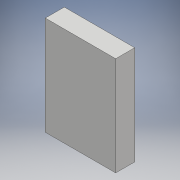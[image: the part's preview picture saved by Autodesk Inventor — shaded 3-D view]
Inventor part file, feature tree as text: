
AUTODESK INVENTOR PART (.ipt)
format: ipt  version: 2018.1 (Build 221171000, 171)  size: 92,672 bytes
history: native  units: mm
features: other x1, extrude x1, shell x1, sketch x1
ambient origin geometry x8: Origin, YZ Plane, XZ Plane, XY Plane, X Axis, Y Axis, Z Axis, Center Point
bodies: Body1 (feature_tree)
feature tree (4):
  other  "ソリッド1"
  extrude  "押し出し1"  Depth=52.0mm
  shell  "シェル2"  Thickness=37.0mm
  sketch  "スケッチ1"
